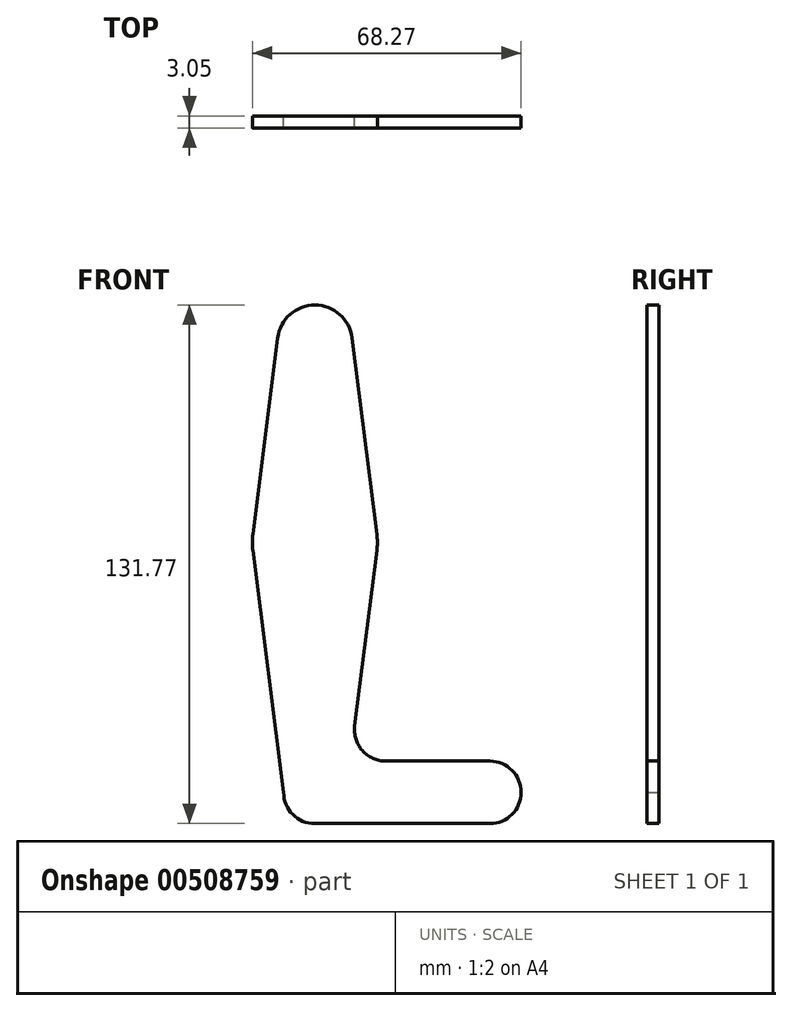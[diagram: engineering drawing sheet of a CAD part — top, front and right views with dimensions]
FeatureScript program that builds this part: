
annotation { "Feature Type Name" : "Feature", "Feature Type Description" : "" }
export const myFeature = defineFeature(function(context is Context, id is Id, definition is map)
    precondition{}
    {
        {
            var Q0;
            Q0=qCreatedBy(makeId("Front.planeOp"),FACE);
            var sketch = newSketch(context, id + "F0", { "sketchPlane" : qUnion([Q0])});
            skCircle(sketch, "E0", {"center": v(0, 0) * mm, "radius": 7.94 * mm});
            skCircle(sketch, "E1", {"center": v(0, 63.5) * mm, "radius": 15.88 * mm});
            skCircle(sketch, "E2", {"center": v(0, 114.3) * mm, "radius": 9.53 * mm});
            skCircle(sketch, "E3", {"center": v(44.45, 0) * mm, "radius": 7.94 * mm});
            skLineSegment(sketch, "E4", {"start": v(0, 114.3) * mm, "end": v(0, 63.5) * mm, "construction": true});
            skLineSegment(sketch, "E5", {"start": v(0, 63.5) * mm, "end": v(0, 0) * mm, "construction": true});
            skLineSegment(sketch, "E6", {"start": v(0, 0) * mm, "end": v(44.45, 0) * mm, "construction": true});
            skLineSegment(sketch, "E7", {"start": v(-9.45, 115.5) * mm, "end": v(-15.75, 65.48) * mm});
            skLineSegment(sketch, "E8", {"start": v(9.45, 115.5) * mm, "end": v(15.75, 65.48) * mm});
            skLineSegment(sketch, "E9", {"start": v(-7.94, 0) * mm, "end": v(-15.75, 61.52) * mm});
            skLineSegment(sketch, "E10", {"start": v(44.45, 7.94) * mm, "end": v(18.01, 7.94) * mm});
            skLineSegment(sketch, "E11", {"start": v(44.45, -7.94) * mm, "end": v(0, -7.94) * mm});
            skLineSegment(sketch, "E12", {"start": v(15.75, 61.52) * mm, "end": v(10.13, 16.88) * mm});
            skCircle(sketch, "E13", {"center": v(0, 114.3) * mm, "radius": 3.18 * mm});
            skCircle(sketch, "E14", {"center": v(0, 63.5) * mm, "radius": 3.18 * mm});
            skCircle(sketch, "E15", {"center": v(0, 0) * mm, "radius": 3.18 * mm});
            skCircle(sketch, "E16", {"center": v(44.45, 0) * mm, "radius": 3.18 * mm});
            skCircle(sketch, "E17", {"center": v(-3.17, 100.03) * mm, "radius": 3.18 * mm});
            skArc(sketch, "E18.filletArc", {"start": v(10.13, 16.88) * mm, "mid": v(12.05, 10.63) * mm, "end": v(18.01, 7.94) * mm});
            skSolve(sketch);
        }
        {
            var Q0;
            Q0=makeQuery(id+"F0.imprint","IMPRINT",FACE,{"disambiguationData":[TD([[makeQuery(id+"F0.imprint","IMPRINT",EDGE,{"derivedFrom":sQuery(id+"F0.wireOp",EDGE,"E16")}),1.0]])]});
            var Q1;
            Q1=makeQuery(id+"F0.imprint","IMPRINT",FACE,{"disambiguationData":[TD([[makeQuery(id+"F0.imprint","IMPRINT",EDGE,{"derivedFrom":sQuery(id+"F0.wireOp",EDGE,"E14")}),1.0]])]});
            var Q2;
            Q2=makeQuery(id+"F0.imprint","IMPRINT",FACE,{"disambiguationData":[TD([[makeQuery(id+"F0.imprint","IMPRINT",EDGE,{"derivedFrom":sQuery(id+"F0.wireOp",EDGE,"E17")}),1.0]])]});
            var Q3;
            Q3=makeQuery(id+"F0.imprint","IMPRINT",FACE,{"disambiguationData":[TD([[makeQuery(id+"F0.imprint","IMPRINT",EDGE,{"derivedFrom":sQuery(id+"F0.wireOp",EDGE,"E15")}),-1.0]])]});
            var Q4;
            Q4=makeQuery(id+"F0.imprint","IMPRINT",FACE,{"disambiguationData":[TD([[makeQuery(id+"F0.imprint","IMPRINT",EDGE,{"derivedFrom":sQuery(id+"F0.wireOp",EDGE,"E16")}),-1.0]])]});
            var Q5;
            Q5=makeQuery(id+"F0.imprint","IMPRINT",FACE,{"disambiguationData":[TD([[makeQuery(id+"F0.imprint","IMPRINT",EDGE,{"derivedFrom":sQuery(id+"F0.wireOp",EDGE,"E13")}),-1.0]])]});
            var Q6;
            Q6=makeQuery(id+"F0.imprint","IMPRINT",FACE,{"disambiguationData":[TD([[makeQuery(id+"F0.imprint","IMPRINT",EDGE,{"derivedFrom":sQuery(id+"F0.wireOp",EDGE,"E14")}),-1.0]])]});
            var Q7;
            {var subQ0=sQuery(id+"F0.wireOp",EDGE,"E9");Q7=makeQuery(id+"F0.imprint","IMPRINT",FACE,{"disambiguationData":[TD([[makeQuery(id+"F0.imprint","IMPRINT",EDGE,{"derivedFrom":subQ0}),-1.0]])]});}
            var Q8;
            {var subQ1=sQuery(id+"F0.wireOp",EDGE,"E7");Q8=makeQuery(id+"F0.imprint","IMPRINT",FACE,{"disambiguationData":[TD([[makeQuery(id+"F0.imprint","IMPRINT",EDGE,{"derivedFrom":subQ1}),1.0]])]});}
            var Q9;
            Q9=makeQuery(id+"F0.imprint","IMPRINT",FACE,{"disambiguationData":[TD([[makeQuery(id+"F0.imprint","IMPRINT",EDGE,{"derivedFrom":sQuery(id+"F0.wireOp",EDGE,"E13")}),1.0]])]});
            var Q10;
            Q10=makeQuery(id+"F0.imprint","IMPRINT",FACE,{"disambiguationData":[TD([[makeQuery(id+"F0.imprint","IMPRINT",EDGE,{"derivedFrom":sQuery(id+"F0.wireOp",EDGE,"E15")}),1.0]])]});
            extrude(context, id + "F1", {"entities" : qUnion([Q0, Q1, Q2, Q3, Q4, Q5, Q6, Q7, Q8, Q9, Q10]), "depth" : 3.05 * mm});
        }
    });
